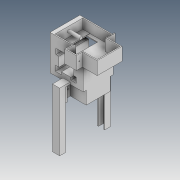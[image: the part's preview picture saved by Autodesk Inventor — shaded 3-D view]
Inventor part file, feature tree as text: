
AUTODESK INVENTOR PART (.ipt)
format: ipt  version: 2021 (Build 250183000, 183)  size: 733,184 bytes
history: native  units: in
note: dims shown in document units (in); Inventor stores cm internally (conversion verified against a paired STEP export)
features: extrude x38, sketch x38, fillet x2, other x1
ambient origin geometry x8: Origin, YZ Plane, XZ Plane, XY Plane, X Axis, Y Axis, Z Axis, Center Point
bodies: Body1 (feature_tree)
feature tree (79):
  other  "Sólido1"
  extrude  "Extrusão1"  Depth=0.1969in
  extrude  "Extrusão2"  Depth=0.3937in
  extrude  "Extrusão3"  Depth=0.0984in
  extrude  "Extrusão4"  Depth=0.1969in
  extrude  "Extrusão5"  Depth=0.3937in
  extrude  "Extrusão6"  Depth=0.0079in
  extrude  "Extrusão7"  Depth=0.0079in
  extrude  "Extrusão10"  Depth=0.0079in
  extrude  "Extrusão11"  Depth=0.0079in
  extrude  "Extrusão12"  Depth=0.0079in
  extrude  "Extrusão13"  Depth=0.0079in
  extrude  "Extrusão25"  Depth=0.0079in
  extrude  "Extrusão26"  Depth=0.0079in
  extrude  "Extrusão27"  Depth=0.1575in
  extrude  "Extrusão28"  Depth=0.0079in
  extrude  "Extrusão29"  Depth=0.0394in
  extrude  "Extrusão30"  Depth=0.0787in
  extrude  "Extrusão31"  Depth=1.1811in TaperAngle=0.0deg
  extrude  "Extrusão32"  Depth=0.3543in
  extrude  "Extrusão34"  Depth=0.1181in
  extrude  "Extrusão35"  Depth=0.1969in TaperAngle=0.0deg
  extrude  "Extrusão36"  Depth=0.0591in
  extrude  "Extrusão37"  Depth=0.2559in
  extrude  "Extrusão38"  Depth=0.0315in TaperAngle=0.0deg
  extrude  "Extrusão39"  Depth=0.0394in
  extrude  "Extrusão41"  Depth=0.0394in
  extrude  "Extrusão43"  Depth=0.0394in
  extrude  "Extrusão44"  Depth=0.0394in
  extrude  "Extrusão46"  Depth=0.0394in TaperAngle=0.0deg
  extrude  "Extrusão47"  Depth=0.1378in
  fillet  "Arredondamento5"  Radius=0.6496in
  fillet  "Arredondamento6"  Radius=0.6496in
  extrude  "Extrusão48"  Depth=0.6693in
  extrude  "Extrusão49"  Depth=0.4724in TaperAngle=0.0deg
  extrude  "Extrusão50"  Depth=0.0394in
  extrude  "Extrusão51"  Depth=0.1969in TaperAngle=0.0deg
  extrude  "Extrusão52"  Depth=0.0394in
  extrude  "Extrusão53"  Depth=0.0394in
  extrude  "Extrusão54"  Depth=0.0787in
  extrude  "Extrusão55"  Depth=0.0787in
  sketch  "Esboço2"  dims[d0=0.1969in d1=0.1969in]
  sketch  "Esboço4"  dims[d2=0.1181in d3=0.3937in]
  sketch  "Esboço5"  dims[d4=0.1969in d5=0.0984in]
  sketch  "Esboço6"  dims[d6=0.3937in d7=0.1969in]
  sketch  "Esboço7"  dims[d8=0.1969in d9=0.3937in]
  sketch  "Esboço8"  dims[d11=0.1969in d12=0.0079in]
  sketch  "Esboço10"  dims[d13=0.0079in d14=0.0079in]
  sketch  "Esboço15"  dims[d15=0.0079in d16=0.0079in]
  sketch  "Esboço16"  dims[d17=0.0079in d19=0.0079in]
  sketch  "Esboço18"  dims[d20=0.0079in d21=0.0079in]
  sketch  "Esboço20"  dims[d22=0.0079in d23=0.0079in]
  sketch  "Esboço38"  dims[d24=0.0079in d25=0.0079in]
  sketch  "Esboço39"  dims[d26=0.0079in d27=0.0079in]
  sketch  "Esboço40"  dims[d28=0.2756in d29=0.1575in]
  sketch  "Esboço41"  dims[d30=0.2756in d31=0.0079in]
  sketch  "Esboço42"  dims[d32=0.0787in d33=0.0394in]
  sketch  "Esboço46"  dims[d34=0.0079in d35=0.0787in]
  sketch  "Esboço47"  dims[d36=0.0394in d37=1.1811in d38=0.0in]
  sketch  "Esboço48"  dims[d39=0.4724in d40=0.3543in]
  sketch  "Esboço53"  dims[d46=0.1969in d47=0.0in d48=0.1181in]
  sketch  "Esboço54"  dims[d49=0.4803in d50=0.0in d51=0.1969in d52=0.0in]
  sketch  "Esboço57"  dims[d53=0.1969in d54=0.0in d55=0.0591in]
  sketch  "Esboço58"  dims[d56=0.1969in d57=0.0in d58=0.2559in]
  sketch  "Esboço59"  dims[d59=0.2559in d60=0.0315in d61=0.0in]
  sketch  "Esboço60"  dims[d68=0.1181in d69=0.0in d70=0.0394in]
  sketch  "Esboço62"  dims[d71=0.0394in d73=0.0394in]
  sketch  "Esboço64"  dims[d74=0.3937in d75=0.0in d76=0.0394in]
  sketch  "Esboço65"  dims[d77=0.0in d78=0.0in d79=0.0394in]
  sketch  "Esboço67"  dims[d80=0.0394in d81=0.0394in d82=0.0in]
  sketch  "Esboço68"  dims[d128=0.1378in d129=0.1378in d131=0.6496in d132=0.6496in]
  sketch  "Esboço69"  dims[d133=0.0197in d134=0.6693in]
  sketch  "Esboço71"  dims[d135=0.0197in d136=0.4724in d137=0.0in]
  sketch  "Esboço72"  dims[d138=0.0394in d139=0.0in d140=0.0394in]
  sketch  "Esboço78"  dims[d141=0.1969in d142=0.0in d143=0.1969in d144=0.0in]
  sketch  "Esboço79"  dims[d145=0.2323in d146=0.0394in]
  sketch  "Esboço80"  dims[d147=0.1083in d148=0.0394in]
  sketch  "Esboço81"  dims[d149=0.1969in d150=0.0in d152=0.0787in]
  sketch  "Esboço82"  dims[d153=0.0394in d154=0.0in d155=0.0787in d156=0.0197in d157=0.0197in d158=0.0787in d159=0.1181in d160=0.0in d161=0.0394in d162=0.1181in d163=0.0394in d164=0.0in d165=0.0in d169=0.0787in d170=0.0315in d171=0.0in d172=0.3937in d173=0.0in d175=0.1181in d176=0.4803in d177=0.0in d178=0.4803in d179=0.0in d180=0.1181in d181=0.1181in d182=0.0394in d183=0.0in d184=0.3724in d185=0.4528in d186=0.8661in d187=0.4528in d188=0.0394in d189=0.0in d199=0.3937in d200=0.0in d206=0.4724in d207=0.0in d208=0.0394in d209=0.0in d210=0.0197in d218=0.0787in d219=0.0787in d220=0.0787in d221=0.0787in d222=0.0787in d223=0.0394in d224=0.0in d225=0.0394in d226=0.0394in d227=0.0394in d228=0.0394in d229=0.0394in d230=0.0394in d231=0.0394in d232=0.4724in d233=0.0in d234=0.0787in d235=0.0787in d236=0.0394in d237=0.0394in d238=0.4724in d239=0.0in d240=0.0394in d241=0.0in d242=0.0394in d243=0.2362in d244=0.0394in d245=0.0394in d246=0.0in d247=0.5512in d248=0.374in d249=0.2047in d250=0.374in d251=0.0787in d252=0.0in d253=0.0394in d254=0.0394in d255=0.0394in d256=0.0394in d257=0.0394in d258=0.0394in d259=0.0394in d260=0.0in d261=2.2441in d262=0.0in d263=0.0394in d264=0.0in d265=0.5906in d266=0.0in d94=0.0197in d95=0.0344in d96=0.0197in d97=0.0344in d123=0.0197in d124=0.0344in d125=0.0197in d126=0.0344in d167=0.0197in d168=0.0344in]
